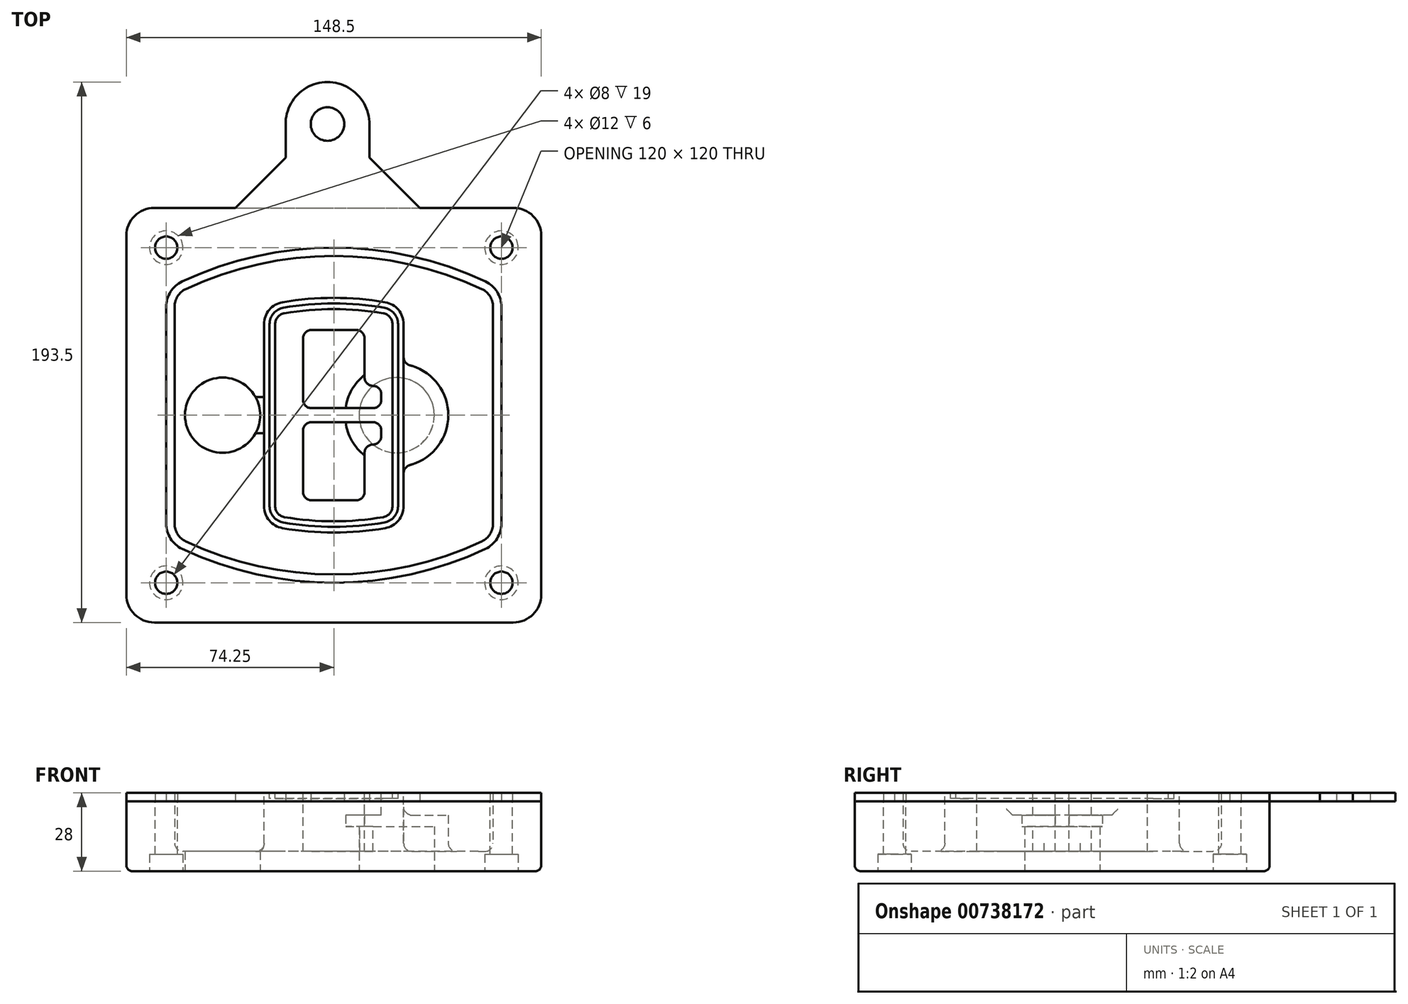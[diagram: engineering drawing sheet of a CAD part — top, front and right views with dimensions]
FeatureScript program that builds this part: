
annotation { "Feature Type Name" : "Feature", "Feature Type Description" : "" }
export const myFeature = defineFeature(function(context is Context, id is Id, definition is map)
    precondition{}
    {
        {
            var Q0;
            Q0=qCreatedBy(makeId("Top.planeOp"),FACE);
            var sketch = newSketch(context, id + "F0", { "sketchPlane" : qUnion([Q0])});
            skPoint(sketch, "E0.rect.middle", {"position": v(0, 0) * mm});
            skLineSegment(sketch, "E1.bottom", {"start": v(-64.25, -74.25) * mm, "end": v(64.25, -74.25) * mm});
            skLineSegment(sketch, "E1.top", {"start": v(-64.25, 74.25) * mm, "end": v(64.25, 74.25) * mm});
            skLineSegment(sketch, "E1.left", {"start": v(-74.25, -64.25) * mm, "end": v(-74.25, 64.25) * mm});
            skLineSegment(sketch, "E1.right", {"start": v(74.25, -64.25) * mm, "end": v(74.25, 64.25) * mm});
            skLineSegment(sketch, "E2", {"start": v(-74.25, 74.25) * mm, "end": v(74.25, -74.25) * mm, "construction": true});
            skLineSegment(sketch, "E3", {"start": v(74.25, 74.25) * mm, "end": v(-74.25, -74.25) * mm, "construction": true});
            skCircle(sketch, "E4", {"center": v(-60, 60) * mm, "radius": 4 * mm});
            skCircle(sketch, "E5", {"center": v(60, 60) * mm, "radius": 4 * mm});
            skCircle(sketch, "E6", {"center": v(60, -60) * mm, "radius": 4 * mm});
            skCircle(sketch, "E7", {"center": v(-60, -60) * mm, "radius": 4 * mm});
            skLineSegment(sketch, "E8", {"start": v(-60, 60) * mm, "end": v(60, 60) * mm, "construction": true});
            skLineSegment(sketch, "E9", {"start": v(60, 60) * mm, "end": v(60, -60) * mm, "construction": true});
            skLineSegment(sketch, "E10", {"start": v(60, -60) * mm, "end": v(-60, -60) * mm, "construction": true});
            skLineSegment(sketch, "E11", {"start": v(-60, -60) * mm, "end": v(-60, 60) * mm, "construction": true});
            skLineSegment(sketch, "E12", {"start": v(-60, 38.83) * mm, "end": v(-60, -38.83) * mm});
            skLineSegment(sketch, "E13", {"start": v(60, 38.83) * mm, "end": v(60, -38.83) * mm});
            skArc(sketch, "E14", {"start": v(54.26, 47.88) * mm, "mid": v(0, 60) * mm, "end": v(-54.26, 47.88) * mm});
            skArc(sketch, "E15", {"start": v(-54.26, -47.88) * mm, "mid": v(0, -60) * mm, "end": v(54.26, -47.88) * mm});
            skLineSegment(sketch, "E16", {"start": v(-60, 0) * mm, "end": v(60, 0) * mm, "construction": true});
            skPoint(sketch, "E17.visualSharp", {"position": v(-60, -45) * mm});
            skArc(sketch, "E17.filletArc", {"start": v(-60, -38.83) * mm, "mid": v(-58.44, -44.2) * mm, "end": v(-54.26, -47.88) * mm});
            skPoint(sketch, "E18.visualSharp", {"position": v(-60, 45) * mm});
            skArc(sketch, "E18.filletArc", {"start": v(-54.26, 47.88) * mm, "mid": v(-58.44, 44.2) * mm, "end": v(-60, 38.83) * mm});
            skPoint(sketch, "E19.visualSharp", {"position": v(60, 45) * mm});
            skArc(sketch, "E19.filletArc", {"start": v(60, 38.83) * mm, "mid": v(58.44, 44.2) * mm, "end": v(54.26, 47.88) * mm});
            skPoint(sketch, "E20.visualSharp", {"position": v(60, -45) * mm});
            skArc(sketch, "E20.filletArc", {"start": v(54.26, -47.88) * mm, "mid": v(58.44, -44.2) * mm, "end": v(60, -38.83) * mm});
            skPoint(sketch, "E21.visualSharp", {"position": v(-74.25, 74.25) * mm});
            skArc(sketch, "E21.filletArc", {"start": v(-64.25, 74.25) * mm, "mid": v(-71.32, 71.32) * mm, "end": v(-74.25, 64.25) * mm});
            skPoint(sketch, "E22.visualSharp", {"position": v(74.25, 74.25) * mm});
            skArc(sketch, "E22.filletArc", {"start": v(74.25, 64.25) * mm, "mid": v(71.32, 71.32) * mm, "end": v(64.25, 74.25) * mm});
            skPoint(sketch, "E23.visualSharp", {"position": v(74.25, -74.25) * mm});
            skArc(sketch, "E23.filletArc", {"start": v(64.25, -74.25) * mm, "mid": v(71.32, -71.32) * mm, "end": v(74.25, -64.25) * mm});
            skPoint(sketch, "E24.visualSharp", {"position": v(-74.25, -74.25) * mm});
            skArc(sketch, "E24.filletArc", {"start": v(-74.25, -64.25) * mm, "mid": v(-71.32, -71.32) * mm, "end": v(-64.25, -74.25) * mm});
            skArc(sketch, "E25.0", {"start": v(57, 38.83) * mm, "mid": v(55.9, 42.58) * mm, "end": v(52.98, 45.17) * mm});
            skLineSegment(sketch, "E25.1", {"start": v(57, 38.83) * mm, "end": v(57, -38.83) * mm});
            skArc(sketch, "E25.2", {"start": v(52.98, -45.17) * mm, "mid": v(55.9, -42.58) * mm, "end": v(57, -38.83) * mm});
            skArc(sketch, "E25.3", {"start": v(-52.98, -45.17) * mm, "mid": v(0, -57) * mm, "end": v(52.98, -45.17) * mm});
            skArc(sketch, "E25.4", {"start": v(-57, -38.83) * mm, "mid": v(-55.9, -42.58) * mm, "end": v(-52.98, -45.17) * mm});
            skArc(sketch, "E25.5", {"start": v(52.98, 45.17) * mm, "mid": v(0, 57) * mm, "end": v(-52.98, 45.17) * mm});
            skLineSegment(sketch, "E25.6", {"start": v(-57, 38.83) * mm, "end": v(-57, -38.83) * mm});
            skArc(sketch, "E25.7", {"start": v(-52.98, 45.17) * mm, "mid": v(-55.9, 42.58) * mm, "end": v(-57, 38.83) * mm});
            skArc(sketch, "E26.0", {"start": v(-55.96, 51.5) * mm, "mid": v(-61.82, 46.33) * mm, "end": v(-64, 38.83) * mm});
            skArc(sketch, "E26.1", {"start": v(55.96, 51.5) * mm, "mid": v(0, 64) * mm, "end": v(-55.96, 51.5) * mm});
            skArc(sketch, "E26.2", {"start": v(64, 38.83) * mm, "mid": v(61.82, 46.33) * mm, "end": v(55.96, 51.5) * mm});
            skLineSegment(sketch, "E26.3", {"start": v(64, 38.83) * mm, "end": v(64, -38.83) * mm});
            skArc(sketch, "E26.4", {"start": v(55.96, -51.5) * mm, "mid": v(61.82, -46.33) * mm, "end": v(64, -38.83) * mm});
            skLineSegment(sketch, "E26.5", {"start": v(-64, 38.83) * mm, "end": v(-64, -38.83) * mm});
            skArc(sketch, "E26.6", {"start": v(-55.96, -51.5) * mm, "mid": v(0, -64) * mm, "end": v(55.96, -51.5) * mm});
            skArc(sketch, "E26.7", {"start": v(-64, -38.83) * mm, "mid": v(-61.82, -46.33) * mm, "end": v(-55.96, -51.5) * mm});
            skSolve(sketch);
        }
        {
            var Q0;
            Q0=makeQuery(id+"F0.imprint","IMPRINT",FACE,{"disambiguationData":[TD([[makeQuery(id+"F0.imprint","IMPRINT",EDGE,{"derivedFrom":sQuery(id+"F0.wireOp",EDGE,"E1.bottom")}),1.0]])]});
            var Q1;
            Q1=makeQuery(id+"F0.imprint","IMPRINT",FACE,{"disambiguationData":[TD([[makeQuery(id+"F0.imprint","IMPRINT",EDGE,{"derivedFrom":sQuery(id+"F0.wireOp",EDGE,"E12")}),1.0]])]});
            var Q2;
            Q2=makeQuery(id+"F0.imprint","IMPRINT",FACE,{"disambiguationData":[TD([[makeQuery(id+"F0.imprint","IMPRINT",EDGE,{"derivedFrom":sQuery(id+"F0.wireOp",EDGE,"E25.0")}),1.0]])]});
            var Q3;
            Q3=makeQuery(id+"F0.imprint","IMPRINT",FACE,{"disambiguationData":[TD([[makeQuery(id+"F0.imprint","IMPRINT",EDGE,{"derivedFrom":sQuery(id+"F0.wireOp",EDGE,"E12")}),-1.0]])]});
            extrude(context, id + "F1", {"entities" : qUnion([Q0, Q1, Q2, Q3]), "oppositeDirection" : true, "depth" : 25 * mm});
        }
        {
            var Q0;
            Q0=makeQuery(id+"F0.imprint","IMPRINT",FACE,{"disambiguationData":[TD([[makeQuery(id+"F0.imprint","IMPRINT",EDGE,{"derivedFrom":sQuery(id+"F0.wireOp",EDGE,"E12")}),1.0]])]});
            extrude(context, id + "F2", {"entities" : qUnion([Q0]), "operationType" : NewBodyOperationType.ADD, "depth" : 3 * mm});
        }
        {
            var Q0;
            Q0=makeQuery(id+"F0.imprint","IMPRINT",FACE,{"disambiguationData":[TD([[makeQuery(id+"F0.imprint","IMPRINT",EDGE,{"derivedFrom":sQuery(id+"F0.wireOp",EDGE,"E25.0")}),1.0]])]});
            extrude(context, id + "F3", {"entities" : qUnion([Q0]), "operationType" : NewBodyOperationType.REMOVE, "oppositeDirection" : true, "depth" : 18 * mm});
        }
        {
            var Q0;
            Q0=makeQuery(id+"F2.opExtrude","CAP_FACE",FACE,{"disambiguationData":[OSD([sQuery(id+"F0.wireOp",EDGE,"E12"),sQuery(id+"F0.wireOp",EDGE,"E13"),sQuery(id+"F0.wireOp",EDGE,"E14"),sQuery(id+"F0.wireOp",EDGE,"E15"),sQuery(id+"F0.wireOp",EDGE,"E17.filletArc"),sQuery(id+"F0.wireOp",EDGE,"E18.filletArc"),sQuery(id+"F0.wireOp",EDGE,"E19.filletArc"),sQuery(id+"F0.wireOp",EDGE,"E20.filletArc"),sQuery(id+"F0.wireOp",EDGE,"E25.0"),sQuery(id+"F0.wireOp",EDGE,"E25.1"),sQuery(id+"F0.wireOp",EDGE,"E25.2"),sQuery(id+"F0.wireOp",EDGE,"E25.3"),sQuery(id+"F0.wireOp",EDGE,"E25.4"),sQuery(id+"F0.wireOp",EDGE,"E25.5"),sQuery(id+"F0.wireOp",EDGE,"E25.6"),sQuery(id+"F0.wireOp",EDGE,"E25.7")])],"isStart":false});
            var sketch = newSketch(context, id + "F4", { "sketchPlane" : qUnion([Q0])});
            skArc(sketch, "E27.0", {"start": v(-18.34, -40.45) * mm, "mid": v(0, -42) * mm, "end": v(18.34, -40.45) * mm});
            skArc(sketch, "E28.0", {"start": v(18.34, 40.45) * mm, "mid": v(0, 42) * mm, "end": v(-18.34, 40.45) * mm});
            skLineSegment(sketch, "E29", {"start": v(-25, 32.57) * mm, "end": v(-25, -32.57) * mm});
            skLineSegment(sketch, "E30", {"start": v(25, 32.57) * mm, "end": v(25, -32.57) * mm});
            skLineSegment(sketch, "E31", {"start": v(-25, 39.1) * mm, "end": v(25, 39.1) * mm, "construction": true});
            skLineSegment(sketch, "E32", {"start": v(-25, -39.1) * mm, "end": v(25, -39.1) * mm, "construction": true});
            skPoint(sketch, "E33.visualSharp", {"position": v(-25, 39.1) * mm});
            skArc(sketch, "E33.filletArc", {"start": v(-18.34, 40.45) * mm, "mid": v(-23.11, 37.73) * mm, "end": v(-25, 32.57) * mm});
            skPoint(sketch, "E34.visualSharp", {"position": v(25, 39.1) * mm});
            skArc(sketch, "E34.filletArc", {"start": v(25, 32.57) * mm, "mid": v(23.11, 37.73) * mm, "end": v(18.34, 40.45) * mm});
            skPoint(sketch, "E35.visualSharp", {"position": v(25, -39.1) * mm});
            skArc(sketch, "E35.filletArc", {"start": v(18.34, -40.45) * mm, "mid": v(23.11, -37.73) * mm, "end": v(25, -32.57) * mm});
            skPoint(sketch, "E36.visualSharp", {"position": v(-25, -39.1) * mm});
            skArc(sketch, "E36.filletArc", {"start": v(-25, -32.57) * mm, "mid": v(-23.11, -37.73) * mm, "end": v(-18.34, -40.45) * mm});
            skArc(sketch, "E37.0", {"start": v(52.98, 45.17) * mm, "mid": v(0, 57) * mm, "end": v(-52.98, 45.17) * mm});
            skArc(sketch, "E37.1", {"start": v(-52.98, 45.17) * mm, "mid": v(-55.9, 42.58) * mm, "end": v(-57, 38.83) * mm});
            skLineSegment(sketch, "E37.2", {"start": v(-57, 38.83) * mm, "end": v(-57, -38.83) * mm});
            skArc(sketch, "E37.3", {"start": v(-57, -38.83) * mm, "mid": v(-55.9, -42.58) * mm, "end": v(-52.98, -45.17) * mm});
            skArc(sketch, "E37.4", {"start": v(-52.98, -45.17) * mm, "mid": v(0, -57) * mm, "end": v(52.98, -45.17) * mm});
            skArc(sketch, "E37.5", {"start": v(52.98, -45.17) * mm, "mid": v(55.9, -42.58) * mm, "end": v(57, -38.83) * mm});
            skLineSegment(sketch, "E37.6", {"start": v(57, 38.83) * mm, "end": v(57, -38.83) * mm});
            skArc(sketch, "E37.7", {"start": v(57, 38.83) * mm, "mid": v(55.9, 42.58) * mm, "end": v(52.98, 45.17) * mm});
            skLineSegment(sketch, "E38.0", {"start": v(23, 32.57) * mm, "end": v(23, -32.57) * mm});
            skArc(sketch, "E38.1", {"start": v(18, -38.48) * mm, "mid": v(21.58, -36.44) * mm, "end": v(23, -32.57) * mm});
            skArc(sketch, "E38.2", {"start": v(-18, -38.48) * mm, "mid": v(0, -40) * mm, "end": v(18, -38.48) * mm});
            skArc(sketch, "E38.3", {"start": v(-23, -32.57) * mm, "mid": v(-21.58, -36.44) * mm, "end": v(-18, -38.48) * mm});
            skLineSegment(sketch, "E38.4", {"start": v(-23, 32.57) * mm, "end": v(-23, -32.57) * mm});
            skArc(sketch, "E38.5", {"start": v(23, 32.57) * mm, "mid": v(21.58, 36.44) * mm, "end": v(18, 38.48) * mm});
            skArc(sketch, "E38.6", {"start": v(-18, 38.48) * mm, "mid": v(-21.58, 36.44) * mm, "end": v(-23, 32.57) * mm});
            skArc(sketch, "E38.7", {"start": v(18, 38.48) * mm, "mid": v(0, 40) * mm, "end": v(-18, 38.48) * mm});
            skArc(sketch, "E39.0", {"start": v(21, 32.57) * mm, "mid": v(20.06, 35.15) * mm, "end": v(17.67, 36.5) * mm});
            skLineSegment(sketch, "E39.1", {"start": v(21, 32.57) * mm, "end": v(21, -32.57) * mm});
            skArc(sketch, "E39.2", {"start": v(17.67, -36.5) * mm, "mid": v(20.06, -35.15) * mm, "end": v(21, -32.57) * mm});
            skArc(sketch, "E39.3", {"start": v(-17.67, -36.5) * mm, "mid": v(0, -38) * mm, "end": v(17.67, -36.5) * mm});
            skArc(sketch, "E39.4", {"start": v(-21, -32.57) * mm, "mid": v(-20.06, -35.15) * mm, "end": v(-17.67, -36.5) * mm});
            skArc(sketch, "E39.5", {"start": v(17.67, 36.5) * mm, "mid": v(0, 38) * mm, "end": v(-17.67, 36.5) * mm});
            skLineSegment(sketch, "E39.6", {"start": v(-21, 32.57) * mm, "end": v(-21, -32.57) * mm});
            skArc(sketch, "E39.7", {"start": v(-17.67, 36.5) * mm, "mid": v(-20.06, 35.15) * mm, "end": v(-21, 32.57) * mm});
            skLineSegment(sketch, "E40", {"start": v(-25, 0) * mm, "end": v(25, 0) * mm, "construction": true});
            skLineSegment(sketch, "E41", {"start": v(-11, 5.5) * mm, "end": v(-11, 27.5) * mm});
            skLineSegment(sketch, "E42", {"start": v(-8, 30.5) * mm, "end": v(8, 30.5) * mm});
            skLineSegment(sketch, "E43", {"start": v(11, 27.5) * mm, "end": v(11, 13.5) * mm});
            skLineSegment(sketch, "E44", {"start": v(14, 10.5) * mm, "end": v(14, 10.5) * mm});
            skLineSegment(sketch, "E45", {"start": v(17, 7.5) * mm, "end": v(17, 5.5) * mm});
            skLineSegment(sketch, "E46", {"start": v(14, 2.5) * mm, "end": v(-8, 2.5) * mm});
            skPoint(sketch, "E47.visualSharp", {"position": v(-11, 30.5) * mm});
            skArc(sketch, "E47.filletArc", {"start": v(-8, 30.5) * mm, "mid": v(-10.12, 29.62) * mm, "end": v(-11, 27.5) * mm});
            skPoint(sketch, "E48.visualSharp", {"position": v(11, 30.5) * mm});
            skArc(sketch, "E48.filletArc", {"start": v(11, 27.5) * mm, "mid": v(10.12, 29.62) * mm, "end": v(8, 30.5) * mm});
            skPoint(sketch, "E49.visualSharp", {"position": v(11, 10.5) * mm});
            skArc(sketch, "E49.filletArc", {"start": v(11, 13.5) * mm, "mid": v(11.88, 11.38) * mm, "end": v(14, 10.5) * mm});
            skPoint(sketch, "E50.visualSharp", {"position": v(17, 10.5) * mm});
            skArc(sketch, "E50.filletArc", {"start": v(17, 7.5) * mm, "mid": v(16.12, 9.62) * mm, "end": v(14, 10.5) * mm});
            skPoint(sketch, "E51.visualSharp", {"position": v(17, 2.5) * mm});
            skArc(sketch, "E51.filletArc", {"start": v(14, 2.5) * mm, "mid": v(16.12, 3.38) * mm, "end": v(17, 5.5) * mm});
            skPoint(sketch, "E52.visualSharp", {"position": v(-11, 2.5) * mm});
            skArc(sketch, "E52.filletArc", {"start": v(-11, 5.5) * mm, "mid": v(-10.12, 3.38) * mm, "end": v(-8, 2.5) * mm});
            skLineSegment(sketch, "E53.0.MirrorCS", {"start": v(14, -2.5) * mm, "end": v(-8, -2.5) * mm});
            skArc(sketch, "E54.0.MirrorCS", {"start": v(-11, -5.5) * mm, "mid": v(-10.12, -3.38) * mm, "end": v(-8, -2.5) * mm});
            skLineSegment(sketch, "E55.0.MirrorCS", {"start": v(-11, -5.5) * mm, "end": v(-11, -27.5) * mm});
            skArc(sketch, "E56.0.MirrorCS", {"start": v(-8, -30.5) * mm, "mid": v(-10.12, -29.62) * mm, "end": v(-11, -27.5) * mm});
            skLineSegment(sketch, "E57.0.MirrorCS", {"start": v(-8, -30.5) * mm, "end": v(8, -30.5) * mm});
            skArc(sketch, "E58.0.MirrorCS", {"start": v(11, -27.5) * mm, "mid": v(10.12, -29.62) * mm, "end": v(8, -30.5) * mm});
            skLineSegment(sketch, "E59.0.MirrorCS", {"start": v(11, -27.5) * mm, "end": v(11, -13.5) * mm});
            skArc(sketch, "E60.0.MirrorCS", {"start": v(11, -13.5) * mm, "mid": v(11.88, -11.38) * mm, "end": v(14, -10.5) * mm});
            skArc(sketch, "E61.0.MirrorCS", {"start": v(17, -7.5) * mm, "mid": v(16.12, -9.62) * mm, "end": v(14, -10.5) * mm});
            skLineSegment(sketch, "E62.0.MirrorCS", {"start": v(17, -7.5) * mm, "end": v(17, -5.5) * mm});
            skArc(sketch, "E63.0.MirrorCS", {"start": v(14, -2.5) * mm, "mid": v(16.12, -3.38) * mm, "end": v(17, -5.5) * mm});
            skSolve(sketch);
        }
        {
            var Q0;
            Q0=makeQuery(id+"F4.imprint","IMPRINT",FACE,{"disambiguationData":[TD([[makeQuery(id+"F4.imprint","IMPRINT",EDGE,{"derivedFrom":sQuery(id+"F4.wireOp",EDGE,"E27.0")}),1.0]])]});
            var Q1;
            Q1=makeQuery(id+"F4.imprint","IMPRINT",FACE,{"disambiguationData":[TD([[makeQuery(id+"F4.imprint","IMPRINT",EDGE,{"derivedFrom":sQuery(id+"F4.wireOp",EDGE,"E38.0")}),-1.0]])]});
            var Q2;
            Q2=makeQuery(id+"F4.imprint","IMPRINT",FACE,{"disambiguationData":[TD([[makeQuery(id+"F4.imprint","IMPRINT",EDGE,{"derivedFrom":sQuery(id+"F4.wireOp",EDGE,"E39.0")}),1.0]])]});
            extrude(context, id + "F5", {"entities" : qUnion([Q0, Q1, Q2]), "operationType" : NewBodyOperationType.ADD, "endBound" : BoundingType.UP_TO_NEXT, "oppositeDirection" : true, "depth" : 25 * mm});
        }
        {
            var Q0;
            Q0=makeQuery(id+"F4.imprint","IMPRINT",FACE,{"disambiguationData":[TD([[makeQuery(id+"F4.imprint","IMPRINT",EDGE,{"derivedFrom":sQuery(id+"F4.wireOp",EDGE,"E38.0")}),-1.0]])]});
            extrude(context, id + "F6", {"entities" : qUnion([Q0]), "operationType" : NewBodyOperationType.REMOVE, "oppositeDirection" : true, "depth" : 2 * mm});
        }
        {
            var Q0;
            Q0=makeQuery(id+"F1.opExtrude","CAP_FACE",FACE,{"disambiguationData":[OSD([sQuery(id+"F0.wireOp",EDGE,"E1.bottom"),sQuery(id+"F0.wireOp",EDGE,"E1.top"),sQuery(id+"F0.wireOp",EDGE,"E1.left"),sQuery(id+"F0.wireOp",EDGE,"E1.right"),sQuery(id+"F0.wireOp",EDGE,"E4"),sQuery(id+"F0.wireOp",EDGE,"E5"),sQuery(id+"F0.wireOp",EDGE,"E6"),sQuery(id+"F0.wireOp",EDGE,"E7"),sQuery(id+"F0.wireOp",EDGE,"E21.filletArc"),sQuery(id+"F0.wireOp",EDGE,"E22.filletArc"),sQuery(id+"F0.wireOp",EDGE,"E23.filletArc"),sQuery(id+"F0.wireOp",EDGE,"E24.filletArc")])],"isStart":false});
            var sketch = newSketch(context, id + "F7", { "sketchPlane" : qUnion([Q0])});
            skCircle(sketch, "E64", {"center": v(22.5, 0) * mm, "radius": 13.47 * mm});
            skCircle(sketch, "E65", {"center": v(-39.81, 0) * mm, "radius": 13.47 * mm});
            skLineSegment(sketch, "E66", {"start": v(74.25, 0) * mm, "end": v(-74.25, 0) * mm});
            skCircle(sketch, "E67", {"center": v(22.5, 0) * mm, "radius": 18.47 * mm});
            skCircle(sketch, "E68", {"center": v(60, -60) * mm, "radius": 6 * mm});
            skCircle(sketch, "E69", {"center": v(-60, -60) * mm, "radius": 6 * mm});
            skCircle(sketch, "E70", {"center": v(-60, 60) * mm, "radius": 6 * mm});
            skCircle(sketch, "E71", {"center": v(60, 60) * mm, "radius": 6 * mm});
            skSolve(sketch);
        }
        {
            var Q0;
            {var subQ1=sQuery(id+"F7.wireOp",EDGE,"E66");var subQ4=sQuery(id+"F7.wireOp",EDGE,"E64");var subQ6=makeQuery(id+"F7.imprint","INTERSECT",VERTEX,{"disambiguationData":[OD(0.0)],"derivedFrom":[subQ4,subQ1]});Q0=makeQuery(id+"F7.imprint","IMPRINT",FACE,{"disambiguationData":[TD([[makeQuery(id+"F7.imprint","IMPRINT",EDGE,{"disambiguationData":[TD([[subQ6,-1.0]])],"derivedFrom":subQ4}),-1.0]])]});}
            var Q1;
            {var subQ0=sQuery(id+"F7.wireOp",EDGE,"E66");var subQ1=sQuery(id+"F7.wireOp",EDGE,"E64");var subQ3=makeQuery(id+"F7.imprint","INTERSECT",VERTEX,{"disambiguationData":[OD(0.0)],"derivedFrom":[subQ1,subQ0]});Q1=makeQuery(id+"F7.imprint","IMPRINT",FACE,{"disambiguationData":[TD([[makeQuery(id+"F7.imprint","IMPRINT",EDGE,{"disambiguationData":[TD([[subQ3,-1.0]])],"derivedFrom":subQ1}),1.0]])]});}
            var Q2;
            {var subQ0=sQuery(id+"F7.wireOp",EDGE,"E66");var subQ1=sQuery(id+"F7.wireOp",EDGE,"E64");var subQ3=makeQuery(id+"F7.imprint","INTERSECT",VERTEX,{"disambiguationData":[OD(0.0)],"derivedFrom":[subQ1,subQ0]});Q2=makeQuery(id+"F7.imprint","IMPRINT",FACE,{"disambiguationData":[TD([[makeQuery(id+"F7.imprint","IMPRINT",EDGE,{"disambiguationData":[TD([[subQ3,1.0]])],"derivedFrom":subQ1}),1.0]])]});}
            var Q3;
            {var subQ1=sQuery(id+"F7.wireOp",EDGE,"E66");var subQ4=sQuery(id+"F7.wireOp",EDGE,"E64");var subQ6=makeQuery(id+"F7.imprint","INTERSECT",VERTEX,{"disambiguationData":[OD(0.0)],"derivedFrom":[subQ4,subQ1]});Q3=makeQuery(id+"F7.imprint","IMPRINT",FACE,{"disambiguationData":[TD([[makeQuery(id+"F7.imprint","IMPRINT",EDGE,{"disambiguationData":[TD([[subQ6,1.0]])],"derivedFrom":subQ4}),-1.0]])]});}
            extrude(context, id + "F8", {"entities" : qUnion([Q0, Q1, Q2, Q3]), "operationType" : NewBodyOperationType.ADD, "oppositeDirection" : true, "depth" : 20 * mm});
        }
        {
            var Q0;
            {var subQ0=sQuery(id+"F7.wireOp",EDGE,"E66");var subQ1=sQuery(id+"F7.wireOp",EDGE,"E64");var subQ3=makeQuery(id+"F7.imprint","INTERSECT",VERTEX,{"disambiguationData":[OD(0.0)],"derivedFrom":[subQ1,subQ0]});Q0=makeQuery(id+"F7.imprint","IMPRINT",FACE,{"disambiguationData":[TD([[makeQuery(id+"F7.imprint","IMPRINT",EDGE,{"disambiguationData":[TD([[subQ3,-1.0]])],"derivedFrom":subQ1}),1.0]])]});}
            var Q1;
            {var subQ0=sQuery(id+"F7.wireOp",EDGE,"E66");var subQ1=sQuery(id+"F7.wireOp",EDGE,"E64");var subQ3=makeQuery(id+"F7.imprint","INTERSECT",VERTEX,{"disambiguationData":[OD(0.0)],"derivedFrom":[subQ1,subQ0]});Q1=makeQuery(id+"F7.imprint","IMPRINT",FACE,{"disambiguationData":[TD([[makeQuery(id+"F7.imprint","IMPRINT",EDGE,{"disambiguationData":[TD([[subQ3,1.0]])],"derivedFrom":subQ1}),1.0]])]});}
            extrude(context, id + "F9", {"entities" : qUnion([Q0, Q1]), "operationType" : NewBodyOperationType.REMOVE, "oppositeDirection" : true, "depth" : 16 * mm});
        }
        {
            var Q0;
            {var subQ0=sQuery(id+"F7.wireOp",EDGE,"E66");var subQ1=sQuery(id+"F7.wireOp",EDGE,"E65");var subQ3=makeQuery(id+"F7.imprint","INTERSECT",VERTEX,{"disambiguationData":[OD(0.0)],"derivedFrom":[subQ1,subQ0]});Q0=makeQuery(id+"F7.imprint","IMPRINT",FACE,{"disambiguationData":[TD([[makeQuery(id+"F7.imprint","IMPRINT",EDGE,{"disambiguationData":[TD([[subQ3,-1.0]])],"derivedFrom":subQ1}),1.0]])]});}
            var Q1;
            {var subQ0=sQuery(id+"F7.wireOp",EDGE,"E66");var subQ1=sQuery(id+"F7.wireOp",EDGE,"E65");var subQ3=makeQuery(id+"F7.imprint","INTERSECT",VERTEX,{"disambiguationData":[OD(0.0)],"derivedFrom":[subQ1,subQ0]});Q1=makeQuery(id+"F7.imprint","IMPRINT",FACE,{"disambiguationData":[TD([[makeQuery(id+"F7.imprint","IMPRINT",EDGE,{"disambiguationData":[TD([[subQ3,1.0]])],"derivedFrom":subQ1}),1.0]])]});}
            extrude(context, id + "F10", {"entities" : qUnion([Q0, Q1]), "operationType" : NewBodyOperationType.REMOVE, "oppositeDirection" : true, "depth" : 25 * mm});
        }
        {
            var Q0;
            Q0=makeQuery(id+"F7.imprint","IMPRINT",FACE,{"disambiguationData":[TD([[makeQuery(id+"F7.imprint","IMPRINT",EDGE,{"derivedFrom":sQuery(id+"F7.wireOp",EDGE,"E68")}),1.0]])]});
            var Q1;
            Q1=makeQuery(id+"F7.imprint","IMPRINT",FACE,{"disambiguationData":[TD([[makeQuery(id+"F7.imprint","IMPRINT",EDGE,{"derivedFrom":makeQuery(id+"F1.opExtrude","CAP_EDGE",EDGE,{"disambiguationData":[OSD([sQuery(id+"F0.wireOp",EDGE,"E5")])],"isStart":false})}),-1.0]])]});
            var Q2;
            Q2=makeQuery(id+"F7.imprint","IMPRINT",FACE,{"disambiguationData":[TD([[makeQuery(id+"F7.imprint","IMPRINT",EDGE,{"derivedFrom":sQuery(id+"F7.wireOp",EDGE,"E69")}),1.0]])]});
            var Q3;
            Q3=makeQuery(id+"F7.imprint","IMPRINT",FACE,{"disambiguationData":[TD([[makeQuery(id+"F7.imprint","IMPRINT",EDGE,{"derivedFrom":makeQuery(id+"F1.opExtrude","CAP_EDGE",EDGE,{"disambiguationData":[OSD([sQuery(id+"F0.wireOp",EDGE,"E4")])],"isStart":false})}),-1.0]])]});
            var Q4;
            Q4=makeQuery(id+"F7.imprint","IMPRINT",FACE,{"disambiguationData":[TD([[makeQuery(id+"F7.imprint","IMPRINT",EDGE,{"derivedFrom":sQuery(id+"F7.wireOp",EDGE,"E70")}),1.0]])]});
            var Q5;
            Q5=makeQuery(id+"F7.imprint","IMPRINT",FACE,{"disambiguationData":[TD([[makeQuery(id+"F7.imprint","IMPRINT",EDGE,{"derivedFrom":makeQuery(id+"F1.opExtrude","CAP_EDGE",EDGE,{"disambiguationData":[OSD([sQuery(id+"F0.wireOp",EDGE,"E7")])],"isStart":false})}),-1.0]])]});
            var Q6;
            Q6=makeQuery(id+"F7.imprint","IMPRINT",FACE,{"disambiguationData":[TD([[makeQuery(id+"F7.imprint","IMPRINT",EDGE,{"derivedFrom":sQuery(id+"F7.wireOp",EDGE,"E71")}),1.0]])]});
            var Q7;
            Q7=makeQuery(id+"F7.imprint","IMPRINT",FACE,{"disambiguationData":[TD([[makeQuery(id+"F7.imprint","IMPRINT",EDGE,{"derivedFrom":makeQuery(id+"F1.opExtrude","CAP_EDGE",EDGE,{"disambiguationData":[OSD([sQuery(id+"F0.wireOp",EDGE,"E6")])],"isStart":false})}),-1.0]])]});
            extrude(context, id + "F11", {"entities" : qUnion([Q0, Q1, Q2, Q3, Q4, Q5, Q6, Q7]), "operationType" : NewBodyOperationType.REMOVE, "oppositeDirection" : true, "depth" : 6 * mm});
        }
        {
            var Q0;
            Q0=makeQuery(id+"F9.boolean.opBoolean","COPY",FACE,{"derivedFrom":makeQuery(id+"F9.opExtrude","CAP_FACE",FACE,{"disambiguationData":[OSD([sQuery(id+"F7.wireOp",EDGE,"E64")])],"isStart":false})});
            var sketch = newSketch(context, id + "F12", { "sketchPlane" : qUnion([Q0])});
            skArc(sketch, "E72.0", {"start": v(11, 14.45) * mm, "mid": v(6.45, 9.13) * mm, "end": v(4.2, 2.5) * mm});
            skArc(sketch, "E72.1", {"start": v(4.2, -2.5) * mm, "mid": v(6.45, -9.13) * mm, "end": v(11, -14.45) * mm});
            skLineSegment(sketch, "E73", {"start": v(4.2, -2.5) * mm, "end": v(14, -2.5) * mm});
            skLineSegment(sketch, "E74.0", {"start": v(14, 2.5) * mm, "end": v(4.2, 2.5) * mm});
            skArc(sketch, "E74.1", {"start": v(14, 2.5) * mm, "mid": v(16.12, 3.38) * mm, "end": v(17, 5.5) * mm});
            skLineSegment(sketch, "E74.2", {"start": v(17, 7.5) * mm, "end": v(17, 5.5) * mm});
            skArc(sketch, "E74.3", {"start": v(17, 7.5) * mm, "mid": v(16.12, 9.62) * mm, "end": v(14, 10.5) * mm});
            skArc(sketch, "E74.4", {"start": v(11, 13.5) * mm, "mid": v(11.88, 11.38) * mm, "end": v(14, 10.5) * mm});
            skLineSegment(sketch, "E74.5", {"start": v(11, 14.45) * mm, "end": v(11, 13.5) * mm});
            skLineSegment(sketch, "E74.7", {"start": v(14, -2.5) * mm, "end": v(4.2, -2.5) * mm});
            skArc(sketch, "E74.8", {"start": v(14, -2.5) * mm, "mid": v(16.12, -3.38) * mm, "end": v(17, -5.5) * mm});
            skLineSegment(sketch, "E74.9", {"start": v(17, -7.5) * mm, "end": v(17, -5.5) * mm});
            skArc(sketch, "E74.10", {"start": v(17, -7.5) * mm, "mid": v(16.12, -9.62) * mm, "end": v(14, -10.5) * mm});
            skArc(sketch, "E74.11", {"start": v(11, -13.5) * mm, "mid": v(11.88, -11.38) * mm, "end": v(14, -10.5) * mm});
            skLineSegment(sketch, "E74.12", {"start": v(11, -14.45) * mm, "end": v(11, -13.5) * mm});
            skPoint(sketch, "E75.orphan", {"position": v(11, -27.5) * mm});
            skPoint(sketch, "E76.orphan", {"position": v(-8, -2.5) * mm});
            skPoint(sketch, "E77.orphan", {"position": v(-8, 2.5) * mm});
            skPoint(sketch, "E78.orphan", {"position": v(11, 27.5) * mm});
            skSolve(sketch);
        }
        {
            var Q0;
            {var subQ7=sQuery(id+"F12.wireOp",EDGE,"E72.0");var subQ14=sQuery(id+"F12.wireOp",EDGE,"E72.1");var subQ16=sQuery(id+"F12.wireOp",EDGE,"E74.1");var subQ18=sQuery(id+"F12.wireOp",EDGE,"E74.8");Q0=qUnion([makeQuery(id+"F12.imprint","IMPRINT",FACE,{"disambiguationData":[TD([[makeQuery(id+"F12.imprint","IMPRINT",EDGE,{"derivedFrom":subQ7}),1.0]])]}),makeQuery(id+"F12.imprint","IMPRINT",FACE,{"disambiguationData":[TD([[makeQuery(id+"F12.imprint","IMPRINT",EDGE,{"derivedFrom":subQ14}),1.0]])]}),makeQuery(id+"F12.imprint","IMPRINT",FACE,{"disambiguationData":[TD([[makeQuery(id+"F12.imprint","IMPRINT",EDGE,{"derivedFrom":subQ16}),1.0]])]}),makeQuery(id+"F12.imprint","IMPRINT",FACE,{"disambiguationData":[TD([[makeQuery(id+"F12.imprint","IMPRINT",EDGE,{"derivedFrom":subQ18}),-1.0]])]})]);}
            var Q1;
            Q1=makeQuery(id+"F5.boolean.opBoolean","SPLIT",FACE,{"disambiguationData":[TD([makeQuery(id+"F5.opExtrude","SWEPT_FACE",FACE,{"disambiguationData":[OSD([sQuery(id+"F4.wireOp",EDGE,"E41")])]})])],"derivedFrom":makeQuery(id+"F3.boolean.opBoolean","COPY",FACE,{"derivedFrom":makeQuery(id+"F3.opExtrude","CAP_FACE",FACE,{"disambiguationData":[OSD([sQuery(id+"F0.wireOp",EDGE,"E25.0"),sQuery(id+"F0.wireOp",EDGE,"E25.1"),sQuery(id+"F0.wireOp",EDGE,"E25.2"),sQuery(id+"F0.wireOp",EDGE,"E25.3"),sQuery(id+"F0.wireOp",EDGE,"E25.4"),sQuery(id+"F0.wireOp",EDGE,"E25.5"),sQuery(id+"F0.wireOp",EDGE,"E25.6"),sQuery(id+"F0.wireOp",EDGE,"E25.7")])],"isStart":false})})});
            extrude(context, id + "F13", {"entities" : qUnion([Q0]), "operationType" : NewBodyOperationType.REMOVE, "endBound" : BoundingType.UP_TO_SURFACE, "endBoundEntityFace" : qUnion([Q1]), "depth" : 25 * mm});
        }
        {
            var Q0;
            Q0=makeQuery(id+"F3.boolean.opBoolean","COPY",EDGE,{"derivedFrom":makeQuery(id+"F3.opExtrude","CAP_EDGE",EDGE,{"disambiguationData":[OSD([sQuery(id+"F0.wireOp",EDGE,"E25.6")])],"isStart":false})});
            var Q1;
            Q1=makeQuery(id+"F8.boolean.opBoolean","INTERSECT",EDGE,{"derivedFrom":[makeQuery(id+"F5.opExtrude","SWEPT_FACE",FACE,{"disambiguationData":[OSD([sQuery(id+"F4.wireOp",EDGE,"E30")])]}),makeQuery(id+"F8.opExtrude","CAP_FACE",FACE,{"disambiguationData":[OSD([sQuery(id+"F7.wireOp",EDGE,"E67")])],"isStart":false})]});
            var Q2;
            Q2=makeQuery(id+"F8.boolean.opBoolean","INTERSECT",EDGE,{"disambiguationData":[OD(1.0)],"derivedFrom":[makeQuery(id+"F5.opExtrude","SWEPT_FACE",FACE,{"disambiguationData":[OSD([sQuery(id+"F4.wireOp",EDGE,"E30")])]}),makeQuery(id+"F8.opExtrude","SWEPT_FACE",FACE,{"disambiguationData":[OSD([sQuery(id+"F7.wireOp",EDGE,"E67")])]})]});
            var Q3;
            {var subQ0=sQuery(id+"F4.wireOp",EDGE,"E30");Q3=makeQuery(id+"F8.boolean.opBoolean","SPLIT",EDGE,{"disambiguationData":[TD([makeQuery(id+"F5.opExtrude","SWEPT_FACE",FACE,{"disambiguationData":[OSD([sQuery(id+"F4.wireOp",EDGE,"E35.filletArc")])]})])],"derivedFrom":makeQuery(id+"F5.opExtrude","CAP_EDGE",EDGE,{"disambiguationData":[OSD([subQ0])],"isStart":false})});}
            var Q4;
            {var subQ0=sQuery(id+"F0.wireOp",EDGE,"E25.7");var subQ1=sQuery(id+"F0.wireOp",EDGE,"E25.1");var subQ2=sQuery(id+"F0.wireOp",EDGE,"E25.6");var subQ3=sQuery(id+"F0.wireOp",EDGE,"E25.5");var subQ4=sQuery(id+"F0.wireOp",EDGE,"E25.4");var subQ5=sQuery(id+"F0.wireOp",EDGE,"E25.0");var subQ6=sQuery(id+"F0.wireOp",EDGE,"E25.2");var subQ7=sQuery(id+"F0.wireOp",EDGE,"E25.3");Q4=makeQuery(id+"F8.boolean.opBoolean","INTERSECT",EDGE,{"derivedFrom":[makeQuery(id+"F5.boolean.opBoolean","SPLIT",FACE,{"disambiguationData":[TD([makeQuery(id+"F2.opExtrude","SWEPT_FACE",FACE,{"disambiguationData":[OSD([subQ5])]})])],"derivedFrom":makeQuery(id+"F3.boolean.opBoolean","COPY",FACE,{"derivedFrom":makeQuery(id+"F3.opExtrude","CAP_FACE",FACE,{"disambiguationData":[OSD([subQ5,subQ1,subQ6,subQ7,subQ4,subQ3,subQ2,subQ0])],"isStart":false})})}),makeQuery(id+"F8.opExtrude","SWEPT_FACE",FACE,{"disambiguationData":[OSD([sQuery(id+"F7.wireOp",EDGE,"E67")])]})]});}
            var Q5;
            Q5=makeQuery(id+"F8.boolean.opBoolean","INTERSECT",EDGE,{"disambiguationData":[OD(0.0)],"derivedFrom":[makeQuery(id+"F5.opExtrude","SWEPT_FACE",FACE,{"disambiguationData":[OSD([sQuery(id+"F4.wireOp",EDGE,"E30")])]}),makeQuery(id+"F8.opExtrude","SWEPT_FACE",FACE,{"disambiguationData":[OSD([sQuery(id+"F7.wireOp",EDGE,"E67")])]})]});
            fillet(context, id + "F14", {"entities" : qUnion([Q0, Q1, Q2, Q3, Q4, Q5]), "radius" : 3 * mm, "tangentPropagation" : true, "allowEdgeOverflow" : false});
        }
        {
            var Q0;
            Q0=makeQuery(id+"F1.opExtrude","CAP_EDGE",EDGE,{"disambiguationData":[OSD([sQuery(id+"F0.wireOp",EDGE,"E1.bottom")])],"isStart":false});
            fillet(context, id + "F15", {"entities" : qUnion([Q0]), "radius" : 2 * mm, "tangentPropagation" : true, "allowEdgeOverflow" : false});
        }
        {
            var Q0;
            {var subQ0=sQuery(id+"F0.wireOp",EDGE,"E21.filletArc");var subQ1=sQuery(id+"F0.wireOp",EDGE,"E7");var subQ2=sQuery(id+"F0.wireOp",EDGE,"E6");var subQ3=sQuery(id+"F0.wireOp",EDGE,"E5");var subQ4=sQuery(id+"F0.wireOp",EDGE,"E4");var subQ5=sQuery(id+"F0.wireOp",EDGE,"E22.filletArc");var subQ6=sQuery(id+"F0.wireOp",EDGE,"E1.bottom");var subQ7=sQuery(id+"F0.wireOp",EDGE,"E1.right");var subQ8=sQuery(id+"F0.wireOp",EDGE,"E1.top");var subQ9=sQuery(id+"F0.wireOp",EDGE,"E1.left");var subQ10=sQuery(id+"F0.wireOp",EDGE,"E23.filletArc");var subQ11=sQuery(id+"F0.wireOp",EDGE,"E24.filletArc");Q0=makeQuery(id+"F2.boolean.opBoolean","SPLIT",FACE,{"disambiguationData":[TD([makeQuery(id+"F1.opExtrude","SWEPT_FACE",FACE,{"disambiguationData":[OSD([subQ6])]})])],"derivedFrom":makeQuery(id+"F1.opExtrude","CAP_FACE",FACE,{"disambiguationData":[OSD([subQ6,subQ8,subQ9,subQ7,subQ4,subQ3,subQ2,subQ1,subQ0,subQ5,subQ10,subQ11])],"isStart":true})});}
            var sketch = newSketch(context, id + "F16", { "sketchPlane" : qUnion([Q0])});
            skLineSegment(sketch, "E79", {"start": v(30.74, 74.25) * mm, "end": v(12.74, 92.25) * mm});
            skLineSegment(sketch, "E80", {"start": v(12.74, 92.25) * mm, "end": v(12.74, 104.25) * mm});
            skLineSegment(sketch, "E81", {"start": v(-35.26, 74.25) * mm, "end": v(-17.26, 92.25) * mm});
            skLineSegment(sketch, "E82", {"start": v(-17.26, 92.25) * mm, "end": v(-17.26, 104.03) * mm});
            skArc(sketch, "E83", {"start": v(12.74, 104.25) * mm, "mid": v(-2.37, 119.25) * mm, "end": v(-17.26, 104.03) * mm});
            skLineSegment(sketch, "E84", {"start": v(-2.26, 104.25) * mm, "end": v(-2.26, 74.25) * mm, "construction": true});
            skCircle(sketch, "E85", {"center": v(-2.26, 104.25) * mm, "radius": 6 * mm});
            skLineSegment(sketch, "E86", {"start": v(-74.25, 0) * mm, "end": v(74.25, 0) * mm, "construction": true});
            skLineSegment(sketch, "E87.MirrorCS", {"start": v(-17.26, 92.25) * mm, "end": v(-17.26, 104.25) * mm});
            skLineSegment(sketch, "E88.MirrorCS", {"start": v(12.74, 92.25) * mm, "end": v(12.74, 104.03) * mm});
            skArc(sketch, "E89.MirrorCS", {"start": v(-17.26, 104.25) * mm, "mid": v(-2.15, 119.25) * mm, "end": v(12.74, 104.03) * mm});
            skLineSegment(sketch, "E90.MirrorCS", {"start": v(69.73, 0) * mm, "end": v(-78.77, 0) * mm, "construction": true});
            skLineSegment(sketch, "E91.MirrorCS", {"start": v(-2.26, -104.25) * mm, "end": v(-2.26, -74.25) * mm, "construction": true});
            skLineSegment(sketch, "E92.MirrorCS", {"start": v(-35.26, -74.25) * mm, "end": v(-17.26, -92.25) * mm});
            skLineSegment(sketch, "E93.MirrorCS", {"start": v(12.74, -92.25) * mm, "end": v(12.74, -104.25) * mm});
            skLineSegment(sketch, "E94.MirrorCS", {"start": v(-17.26, -92.25) * mm, "end": v(-17.26, -104.03) * mm});
            skArc(sketch, "E95.MirrorCS", {"start": v(12.74, -104.25) * mm, "mid": v(-2.37, -119.25) * mm, "end": v(-17.26, -104.03) * mm});
            skCircle(sketch, "E96.MirrorC", {"center": v(-2.26, -104.25) * mm, "radius": 6 * mm});
            skLineSegment(sketch, "E97.MirrorCS", {"start": v(30.74, -74.25) * mm, "end": v(12.74, -92.25) * mm});
            skLineSegment(sketch, "E98.MirrorCS", {"start": v(12.74, -92.25) * mm, "end": v(12.74, -104.03) * mm});
            skArc(sketch, "E99.MirrorCS", {"start": v(-17.26, -104.25) * mm, "mid": v(-2.15, -119.25) * mm, "end": v(12.74, -104.03) * mm});
            skLineSegment(sketch, "E100.MirrorCS", {"start": v(-17.26, -92.25) * mm, "end": v(-17.26, -104.25) * mm});
            skSolve(sketch);
        }
        {
            var Q0;
            {var subQ1=sQuery(id+"F16.wireOp",EDGE,"E81");Q0=makeQuery(id+"F16.imprint","IMPRINT",FACE,{"disambiguationData":[TD([[makeQuery(id+"F16.imprint","IMPRINT",EDGE,{"derivedFrom":subQ1}),-1.0]])]});}
            var Q1;
            Q1=makeQuery(id+"F16.imprint","IMPRINT",FACE,{"disambiguationData":[TD([[makeQuery(id+"F16.imprint","IMPRINT",EDGE,{"derivedFrom":makeQuery(id+"F1.opExtrude","CAP_EDGE",EDGE,{"disambiguationData":[OSD([sQuery(id+"F0.wireOp",EDGE,"E1.left")])],"isStart":true})}),-1.0]])]});
            var Q2;
            Q2=makeQuery(id+"F16.imprint","IMPRINT",FACE,{"disambiguationData":[TD([[makeQuery(id+"F16.imprint","IMPRINT",EDGE,{"derivedFrom":sQuery(id+"F16.wireOp",EDGE,"E94.MirrorCS")}),1.0]])]});
            var Q3;
            Q3=makeQuery(id+"F2.opExtrude","CAP_FACE",FACE,{"disambiguationData":[OSD([sQuery(id+"F0.wireOp",EDGE,"E12"),sQuery(id+"F0.wireOp",EDGE,"E13"),sQuery(id+"F0.wireOp",EDGE,"E14"),sQuery(id+"F0.wireOp",EDGE,"E15"),sQuery(id+"F0.wireOp",EDGE,"E17.filletArc"),sQuery(id+"F0.wireOp",EDGE,"E18.filletArc"),sQuery(id+"F0.wireOp",EDGE,"E19.filletArc"),sQuery(id+"F0.wireOp",EDGE,"E20.filletArc"),sQuery(id+"F0.wireOp",EDGE,"E25.0"),sQuery(id+"F0.wireOp",EDGE,"E25.1"),sQuery(id+"F0.wireOp",EDGE,"E25.2"),sQuery(id+"F0.wireOp",EDGE,"E25.3"),sQuery(id+"F0.wireOp",EDGE,"E25.4"),sQuery(id+"F0.wireOp",EDGE,"E25.5"),sQuery(id+"F0.wireOp",EDGE,"E25.6"),sQuery(id+"F0.wireOp",EDGE,"E25.7")])],"isStart":false});
            extrude(context, id + "F17", {"entities" : qUnion([Q0, Q1, Q2]), "endBound" : BoundingType.UP_TO_SURFACE, "depth" : 25 * mm, "endBoundEntityFace" : qUnion([Q3]), "offsetDistance" : 25 * mm});
        }
    });
